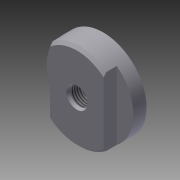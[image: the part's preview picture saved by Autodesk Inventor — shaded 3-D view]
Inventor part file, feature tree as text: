
AUTODESK INVENTOR PART (.ipt)
format: ipt  version: 2014 SP1 (Build 180222100, 222)  size: 108,032 bytes
history: native  units: in
note: dims shown in document units (in); Inventor stores cm internally (conversion verified against a paired STEP export)
features: extrude x2, sketch x2, hole x1, chamfer x1
ambient origin geometry x8: Origin, YZ Plane, XZ Plane, XY Plane, X Axis, Y Axis, Z Axis, Center Point
bodies: Solid1 (feature_tree)
feature tree (6):
  extrude  "Extrusion1"  Depth=0.312in TaperAngle=0.0deg
  extrude  "Extrusion2"  Depth=0.312in TaperAngle=0.0deg
  hole  "Hole1"  [1 undecoded]
  chamfer  "Chamfer1"  Distance=0.0625in Angle=45.0deg
  sketch  "Sketch1"  dims[d0=2.062in d1=0.312in d2=0.0in]
  sketch  "Sketch2"  dims[d5=1.272in d6=0.312in d7=0.0in d8=1.0in d9=1.0in d10=0.422in d11=0.395in d12=0.0246in d13=0.423in d14=0.5in d15=0.25in d16=45.0deg d17=0.75in d18=0.8108in d19=0.0625in d20=0.125in d21=45.0deg]
note: 1 required parameter value undecoded (feature->parameter linkage not recoverable at this tier; creation-order binding heuristic only, values carry confidence <= 0.55)
